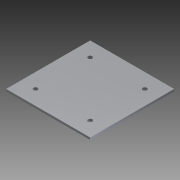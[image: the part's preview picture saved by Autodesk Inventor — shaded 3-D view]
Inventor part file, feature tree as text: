
AUTODESK INVENTOR PART (.ipt)
format: ipt  version: 2011 (Build 150239000, 239)  size: 90,112 bytes
history: native  units: in
note: dims shown in document units (in); Inventor stores cm internally (conversion verified against a paired STEP export)
features: sketch x3, extrude x2
ambient origin geometry x8: Origin, YZ Plane, XZ Plane, XY Plane, X Axis, Y Axis, Z Axis, Center Point
bodies: Solid1 (feature_tree)
feature tree (5):
  sketch  "Sketch1"  dims[d0=20.0in d1=20.0in]
  extrude  "Extrusion1"  Depth=20.0in
  extrude  "Extrusion2"  Depth=3.5in
  sketch  "Sketch2"  dims[d2=0.5in d3=0.0in d4=3.5in]
  sketch  "Sketch3"  dims[d5=3.5in d6=3.5in d7=3.5in d8=3.5in d9=3.5in d10=3.5in d11=3.5in d12=1.0in d13=1.0in d14=1.0in d15=1.0in d16=0.5in d17=0.0in]
